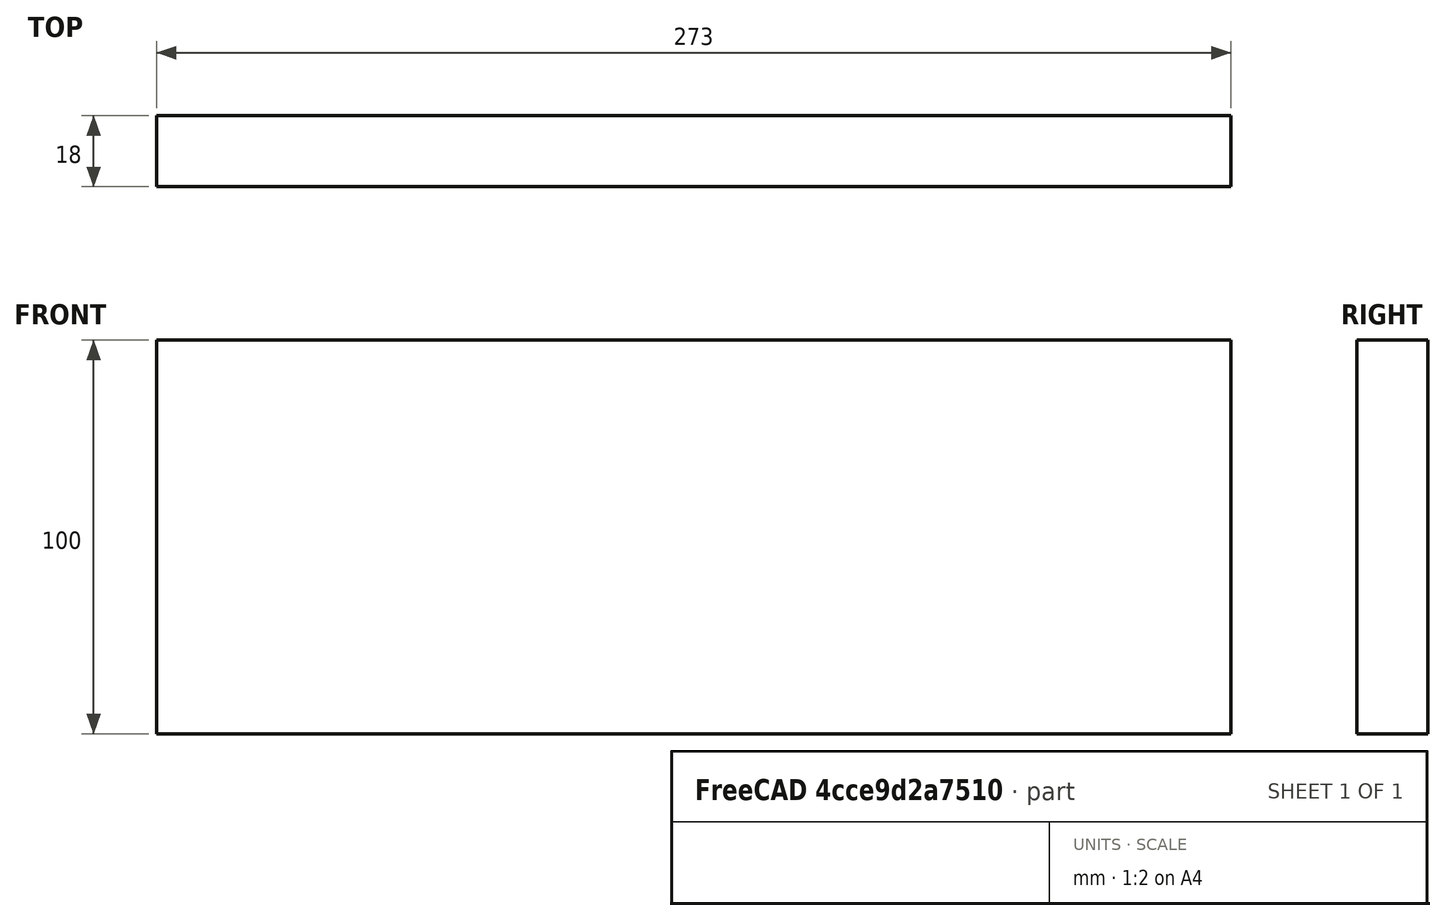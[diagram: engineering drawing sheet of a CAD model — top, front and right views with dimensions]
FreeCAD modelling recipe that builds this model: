
FCSTD DOCUMENT  (FreeCAD 0.18R4 (GitTag))
Label: small_front
License: All rights reserved
LicenseURL: http://en.wikipedia.org/wiki/All_rights_reserved
objects: Sketcher::SketchObject×1, PartDesign::Pad×1, PartDesign::Body×1
note: 4 computed .brp shape members not serialized (recipe doc carries the construction recipe); baked Part::Feature solids carry a one-line shape summary decoded from their .brp

FEATURE [Sketcher::SketchObject] Sketch
  MapMode = 5
  Placement = pos=(0,0,0) rot=(1,0,0;1.5708rad)
  Support = -> [XZ_Plane]
  sketch-geometry (4):
    g0: LineSegment StartX=0 StartY=0 StartZ=0 EndX=-273 EndY=0 EndZ=0
    g1: LineSegment StartX=-273 StartY=0 StartZ=0 EndX=-273 EndY=100 EndZ=0
    g2: LineSegment StartX=-273 StartY=100 StartZ=0 EndX=0 EndY=100 EndZ=0
    g3: LineSegment StartX=0 StartY=100 StartZ=0 EndX=0 EndY=0 EndZ=0
  constraints (11):
    c: Coincident(g0,g1)
    c: Coincident(g1,g2)
    c: Coincident(g2,g3)
    c: Coincident(g3,g0)
    c: Horizontal(g0)
    c: Horizontal(g2)
    c: Vertical(g1)
    c: Vertical(g3)
    c: Coincident(g0,g-1)
    c: DistanceY(g3,g3) = 100
    c: DistanceX(g0,g0) = 273
FEATURE [PartDesign::Pad] Pad
  Length = 18
  Length2 = 100
  Placement = pos=(0,0,0) rot=(1,0,0;1.5708rad)
  Profile = -> Sketch
  Type = 0
FEATURE [PartDesign::Body] Body
  Group = -> [Sketch,Pad]
  Origin = -> Origin
  Tip = -> Pad
